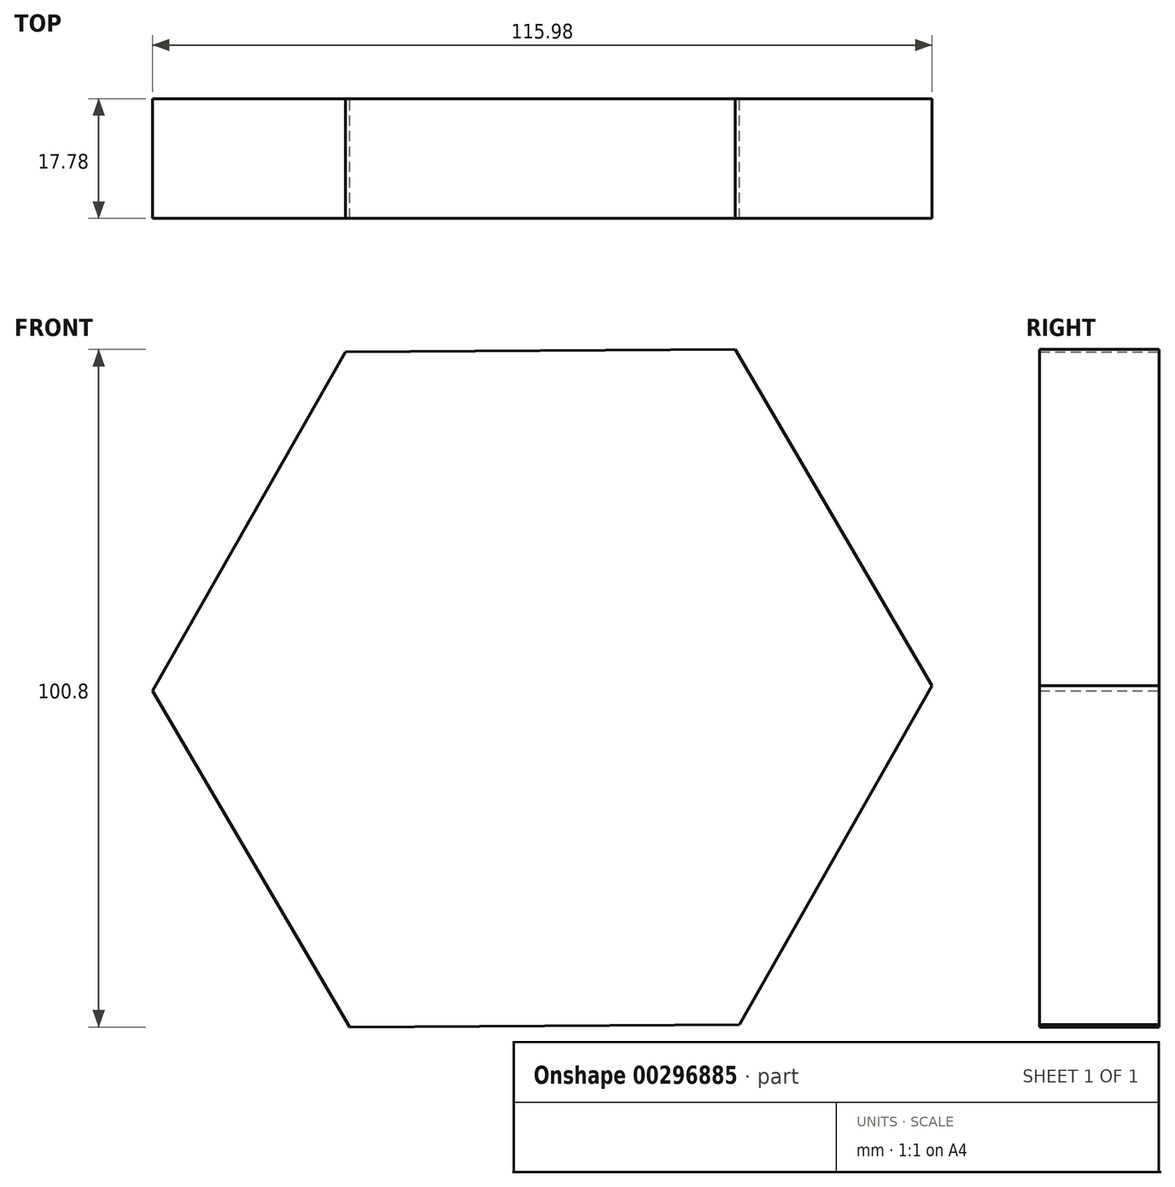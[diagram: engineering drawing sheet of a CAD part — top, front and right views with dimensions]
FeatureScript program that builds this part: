
annotation { "Feature Type Name" : "Feature", "Feature Type Description" : "" }
export const myFeature = defineFeature(function(context is Context, id is Id, definition is map)
    precondition{}
    {
        {
            var Q0;
            Q0=qCreatedBy(makeId("Front.planeOp"),FACE);
            var sketch = newSketch(context, id + "F0", { "sketchPlane" : qUnion([Q0])});
            skCircle(sketch, "E0.cCircle", {"center": v(0, 0) * mm, "radius": 50.22 * mm, "construction": true});
            skLineSegment(sketch, "E0.0", {"start": v(28.67, 50.4) * mm, "end": v(57.99, 0.37) * mm});
            skLineSegment(sketch, "E0.1", {"start": v(57.99, 0.37) * mm, "end": v(29.31, -50.03) * mm});
            skLineSegment(sketch, "E0.2", {"start": v(29.31, -50.03) * mm, "end": v(-28.67, -50.4) * mm});
            skLineSegment(sketch, "E0.3", {"start": v(-28.67, -50.4) * mm, "end": v(-57.99, -0.37) * mm});
            skLineSegment(sketch, "E0.4", {"start": v(-57.99, -0.37) * mm, "end": v(-29.31, 50.03) * mm});
            skLineSegment(sketch, "E0.5", {"start": v(-29.31, 50.03) * mm, "end": v(28.67, 50.4) * mm});
            skPoint(sketch, "E0.0.midPoint", {"position": v(43.33, 25.39) * mm});
            skSolve(sketch);
        }
        {
            var Q0;
            Q0=makeQuery(id+"F0.imprint","IMPRINT",FACE,{"disambiguationData":[TD([[makeQuery(id+"F0.imprint","IMPRINT",EDGE,{"derivedFrom":sQuery(id+"F0.wireOp",EDGE,"E0.0")}),-1.0]])]});
            extrude(context, id + "F1", {"entities" : qUnion([Q0]), "endBound" : BoundingType.SYMMETRIC, "depth" : 17.78 * mm});
        }
    });
